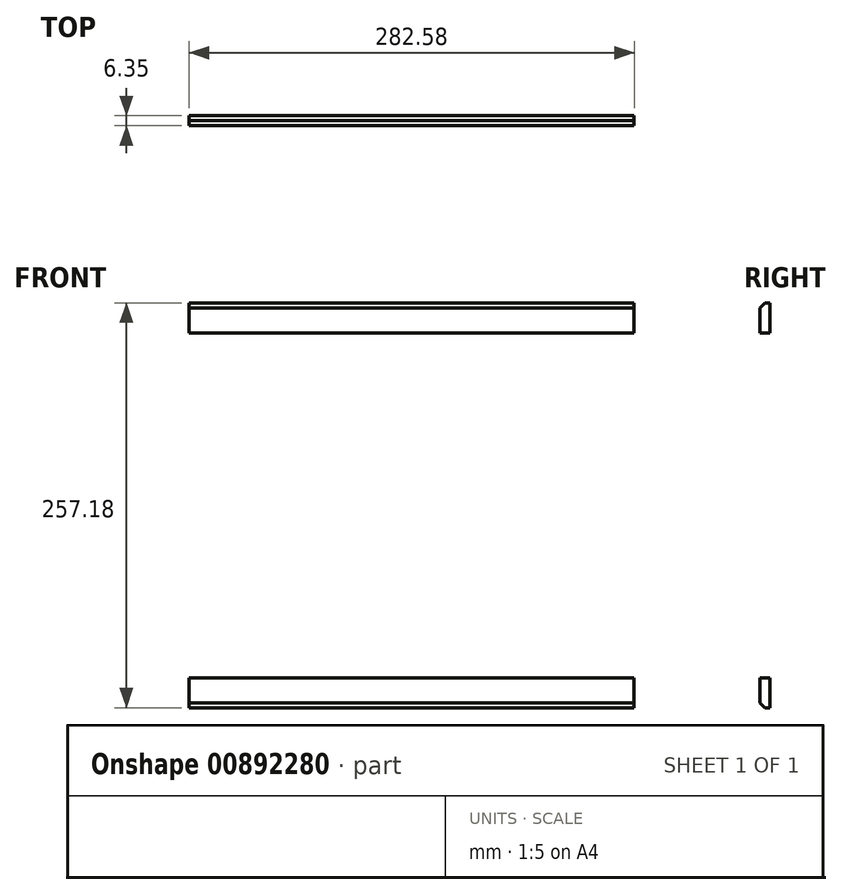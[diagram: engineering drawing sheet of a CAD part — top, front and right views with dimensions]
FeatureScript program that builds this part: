
annotation { "Feature Type Name" : "Feature", "Feature Type Description" : "" }
export const myFeature = defineFeature(function(context is Context, id is Id, definition is map)
    precondition{}
    {
        {
            var Q0;
            Q0=qCreatedBy(makeId("Front.planeOp"),FACE);
            var sketch = newSketch(context, id + "F0", { "sketchPlane" : qUnion([Q0])});
            skLineSegment(sketch, "E0.bottom", {"start": v(-141.29, 128.59) * mm, "end": v(141.29, 128.59) * mm});
            skLineSegment(sketch, "E0.top", {"start": v(-141.29, 109.54) * mm, "end": v(141.29, 109.54) * mm});
            skLineSegment(sketch, "E0.left", {"start": v(-141.29, 128.59) * mm, "end": v(-141.29, 109.54) * mm});
            skLineSegment(sketch, "E0.right", {"start": v(141.29, 128.59) * mm, "end": v(141.29, 109.54) * mm});
            skPoint(sketch, "E1.firstSnap0", {"position": v(0, 109.54) * mm});
            skLineSegment(sketch, "E1.top", {"start": v(-50.68, 128.59) * mm, "end": v(0, 128.59) * mm});
            skSolve(sketch);
        }
        {
            var Q0;
            Q0=makeQuery(id+"F0.imprint","IMPRINT",FACE,{"disambiguationData":[TD([[makeQuery(id+"F0.imprint","IMPRINT",EDGE,{"derivedFrom":sQuery(id+"F0.wireOp",EDGE,"E0.bottom")}),-1.0]])]});
            extrude(context, id + "F1", {"entities" : qUnion([Q0]), "depth" : 6.35 * mm, "offsetDistance" : 25.4 * mm});
        }
        {
            var Q0;
            Q0=makeQuery(id+"F1.opExtrude","CAP_EDGE",EDGE,{"disambiguationData":[OSD([sQuery(id+"F0.wireOp",EDGE,"E0.bottom")])],"isStart":false});
            chamfer(context, id + "F2", {"entities" : qUnion([Q0]), "width" : 3.17 * mm, "tangentPropagation" : true});
        }
        {
            var Q0;
            Q0=makeQuery(id+"F1.opExtrude","SWEPT_BODY",BODY,{"disambiguationData":[OSD([sQuery(id+"F0.wireOp",EDGE,"E0.bottom"),sQuery(id+"F0.wireOp",EDGE,"E0.top"),sQuery(id+"F0.wireOp",EDGE,"E0.left"),sQuery(id+"F0.wireOp",EDGE,"E0.right"),sQuery(id+"F0.wireOp",EDGE,"E1.top")])]});
            var Q1;
            Q1=qCreatedBy(makeId("Top.planeOp"),FACE);
            mirror(context, id + "F3", {"entities" : qUnion([Q0]), "mirrorPlane" : qUnion([Q1])});
        }
    });
